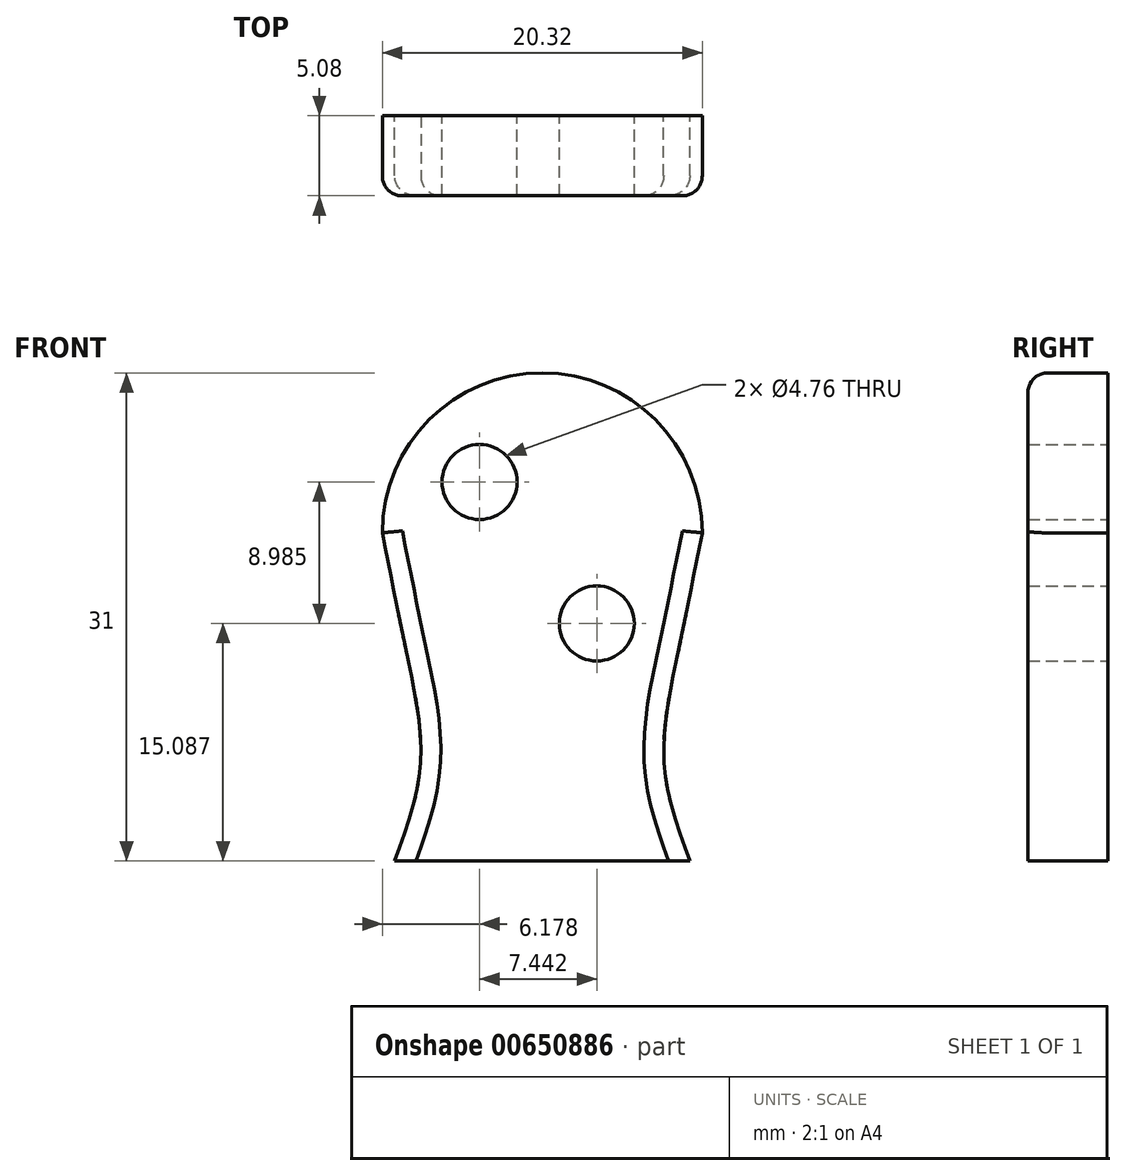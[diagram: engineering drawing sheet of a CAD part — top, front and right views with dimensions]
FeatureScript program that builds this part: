
annotation { "Feature Type Name" : "Feature", "Feature Type Description" : "" }
export const myFeature = defineFeature(function(context is Context, id is Id, definition is map)
    precondition{}
    {
        {
            var Q0;
            Q0=qCreatedBy(makeId("Front.planeOp"),FACE);
            var sketch = newSketch(context, id + "F0", { "sketchPlane" : qUnion([Q0])});
            skCircle(sketch, "E0", {"center": v(-3.98, -1.6) * mm, "radius": 2.38 * mm});
            skCircle(sketch, "E1", {"center": v(3.46, -10.58) * mm, "radius": 2.38 * mm});
            skArc(sketch, "E2", {"start": v(10.16, -4.83) * mm, "mid": v(0, 5.33) * mm, "end": v(-10.16, -4.83) * mm});
            skFitSpline(sketch, "E3", {"points": [v(-10.16, -4.83) * mm, v(-8.63, -12.42) * mm, v(-7.74, -19.44) * mm, v(-9.38, -25.67) * mm], "startDerivative": vector(4.32, -21.85) * mm, "endDerivative": vector(-7.08, -19.25) * mm});
            skFitSpline(sketch, "E4.MirrorCS", {"points": [v(10.16, -4.83) * mm, v(8.63, -12.42) * mm, v(7.74, -19.44) * mm, v(9.38, -25.67) * mm], "startDerivative": vector(-4.32, -21.85) * mm, "endDerivative": vector(7.08, -19.25) * mm});
            skLineSegment(sketch, "E5", {"start": v(9.38, -25.67) * mm, "end": v(-9.38, -25.67) * mm});
            skSolve(sketch);
        }
        {
            var Q0;
            Q0=makeQuery(id+"F0.imprint","IMPRINT",FACE,{"disambiguationData":[TD([[makeQuery(id+"F0.imprint","IMPRINT",EDGE,{"derivedFrom":sQuery(id+"F0.wireOp",EDGE,"E0")}),-1.0]])]});
            extrude(context, id + "F1", {"entities" : qUnion([Q0]), "depth" : 5.08 * mm, "offsetDistance" : 25.4 * mm});
        }
        {
            var Q0;
            Q0=makeQuery(id+"F1.opExtrude","CAP_EDGE",EDGE,{"disambiguationData":[OSD([sQuery(id+"F0.wireOp",EDGE,"E2")])],"isStart":false});
            var Q1;
            Q1=makeQuery(id+"F1.opExtrude","CAP_EDGE",EDGE,{"disambiguationData":[OSD([sQuery(id+"F0.wireOp",EDGE,"E3")])],"isStart":false});
            var Q2;
            Q2=makeQuery(id+"F1.opExtrude","CAP_EDGE",EDGE,{"disambiguationData":[OSD([sQuery(id+"F0.wireOp",EDGE,"E4.MirrorCS")])],"isStart":false});
            fillet(context, id + "F2", {"entities" : qUnion([Q0, Q1, Q2]), "radius" : 1.27 * mm, "tangentPropagation" : true, "allowEdgeOverflow" : false});
        }
    });
